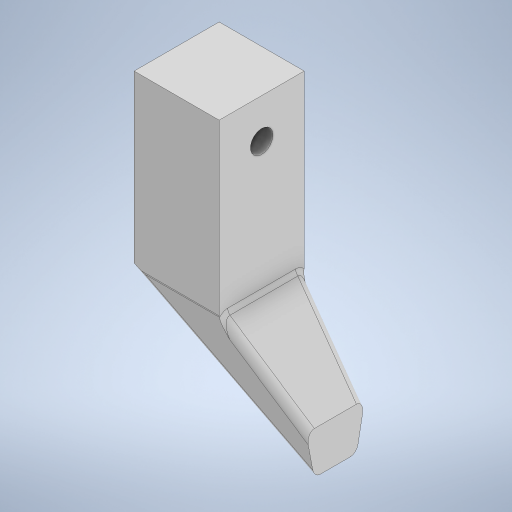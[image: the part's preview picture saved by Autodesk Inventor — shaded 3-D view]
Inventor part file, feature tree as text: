
AUTODESK INVENTOR PART (.ipt)
format: ipt  version: 2024 (Build 280153000, 153)  size: 281,088 bytes
history: native  units: in
note: dims shown in document units (in); Inventor stores cm internally (conversion verified against a paired STEP export)
features: extrude x3, sketch x3, fillet x1
ambient origin geometry x8: Origin, YZ Plane, XZ Plane, XY Plane, X Axis, Y Axis, Z Axis, Center Point
bodies: Solid1 (feature_tree)
feature tree (7):
  extrude  "Extrusion1"  Depth=1.5in
  extrude  "Extrusion2"  Depth=2.0in
  extrude  "Extrusion3"  Depth=1.5in TaperAngle=0.0deg
  fillet  "Fillet1"  Radius=0.375in
  sketch  "Sketch1"  dims[d0=3.0in d1=1.5in]
  sketch  "Sketch3"  dims[d3=2.8in d4=2.0in]
  sketch  "Sketch4"  dims[d5=0.75in d6=1.5in d7=0.0in d9=0.375in d10=1.5in d11=0.0in d12=1.3in d13=0.3976in d14=0.7in d15=1.0in d16=0.0in d17=0.125in]
